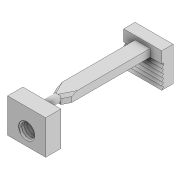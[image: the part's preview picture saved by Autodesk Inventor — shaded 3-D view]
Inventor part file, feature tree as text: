
AUTODESK INVENTOR PART (.ipt)
format: ipt  version: 2021 (Build 250183000, 183)  size: 223,744 bytes
history: native  units: mm
features: thread x1
ambient origin geometry x8: Origin, YZ Plane, XZ Plane, XY Plane, X Axis, Y Axis, Z Axis, Center Point
bodies: Solid1 (feature_tree)
feature tree (1):
  thread  "Gewinde1"  [1 undecoded]
note: 1 required parameter value undecoded (feature->parameter linkage not recoverable at this tier; creation-order binding heuristic only, values carry confidence <= 0.55)
